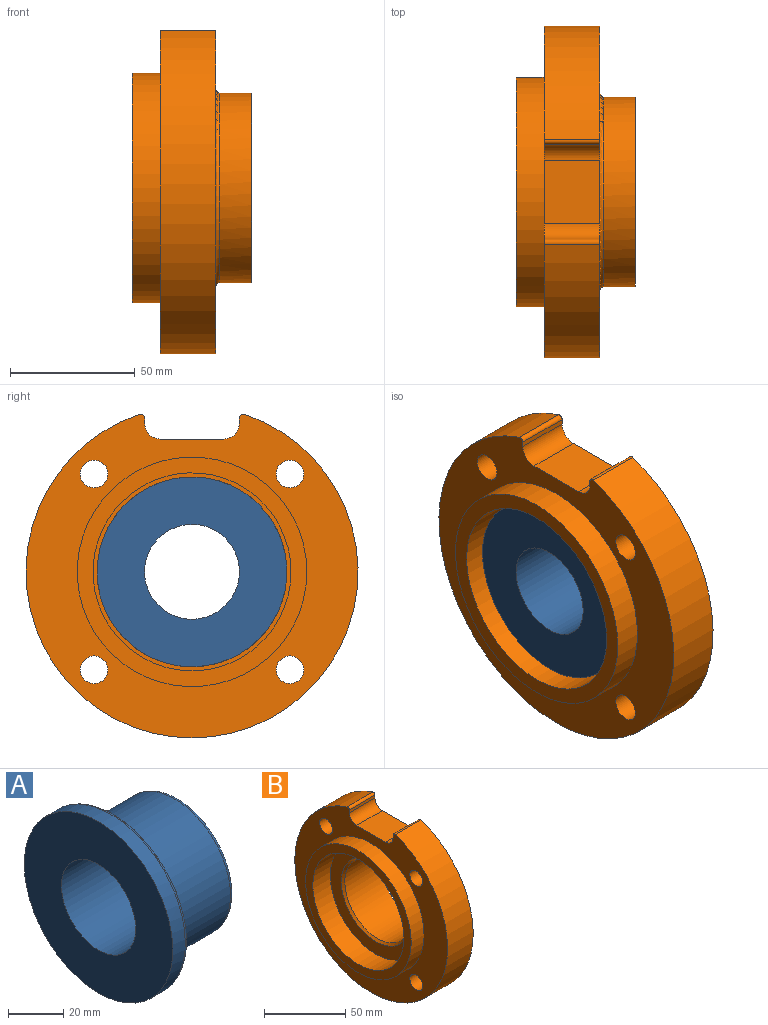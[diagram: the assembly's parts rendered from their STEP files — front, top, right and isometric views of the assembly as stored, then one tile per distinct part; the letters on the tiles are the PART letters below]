
ASSEMBLY  parts=2 mates=1
PART A: 9 faces, bbox 40.6x82.5x82.5 mm
  f0: cylinder r=19.05mm len=40.64mm, axis (-1,0,0), area 4864.4mm2, adj f3,f5
  f1: cylinder r=38.1mm len=76.2mm, axis (-1,0,0), area 1520.1mm2, adj f3,f8
  f2: plane 73.15x73.15mm, normal (1,0,0), area 1356.7mm2, adj f6,f8
  f3: plane 76.2x76.2mm, normal (-1,0,0), area 3420.3mm2, adj f0,f1
  f4: cylinder r=28.57mm len=57.15mm, axis (-1,0,0), area 5335.6mm2, adj f6,f7
  f5: plane 54.1x54.1mm, normal (1,0,0), area 1158.8mm2, adj f0,f7
  f6: torus R=30.1mm, axis (1,0,0), area 438.1mm2, adj f2,f4
  f7: torus R=27.05mm, axis (1,0,0), area 421.5mm2, adj f4,f5
  f8: torus R=36.58mm, axis (1,0,0), area 564.7mm2, adj f1,f2
PART B: 23 faces, bbox 47.8x133.4x130 mm
  f0: cylinder r=28.57mm len=57.15mm, axis (-1,0,0), area 5563.6mm2, adj f16,f22
  f1: plane 25.4x22.35mm, normal (0,0,1), area 567.7mm2, adj f2,f6,f7,f8
  f2: cylinder r=6.35mm len=22.35mm, axis (-1,0,0), area 223mm2, adj f1,f3,f7,f8
  f3: plane 22.35x2.13mm, normal (0,1,0), area 47.5mm2, adj f2,f7,f8,f9
  f4: cylinder r=66.67mm len=133.35mm, axis (-1,0,0), area 8406.3mm2, adj f7,f8,f9,f10
  f5: plane 22.35x2.13mm, normal (0,-1,0), area 47.5mm2, adj f6,f7,f8,f10
  f6: cylinder r=6.35mm len=22.35mm, axis (-1,0,0), area 223mm2, adj f1,f5,f7,f8
  f7: plane 133.35x130.02mm, normal (1,0,0), area 8187.9mm2, adj f1,f2,f3,f4,f5,f6,f9,f10
  f8: plane 133.35x130.02mm, normal (-1,0,0), area 6443.6mm2, adj f1,f2,f3,f4,f5,f6,f9,f10
  f9: cylinder r=1.52mm len=22.35mm, axis (-1,0,0), area 64.5mm2, adj f3,f4,f7,f8
  f10: cylinder r=1.52mm len=22.35mm, axis (-1,0,0), area 64.5mm2, adj f4,f5,f7,f8
  f11: cylinder r=5.56mm len=22.35mm, axis (1,0,0), area 780.3mm2, adj f7,f8
  f12: cylinder r=5.56mm len=22.35mm, axis (1,0,0), area 780.3mm2, adj f7,f8
  f13: cylinder r=5.56mm len=22.35mm, axis (1,0,0), area 780.3mm2, adj f7,f8
  f14: cylinder r=5.56mm len=22.35mm, axis (1,0,0), area 780.3mm2, adj f7,f8
  f15: cylinder r=38.1mm len=76.2mm, axis (-1,0,0), area 3040.2mm2, adj f16,f17
  f16: plane 76.2x76.2mm, normal (1,0,0), area 1995.2mm2, adj f0,f15
  f17: torus R=39.62mm, axis (1,0,0), area 581.4mm2, adj f7,f15
  f18: plane 92.2x92.2mm, normal (-1,0,0), area 1712.7mm2, adj f19,f20
  f19: cylinder r=46.1mm len=92.2mm, axis (1,0,0), area 3237.3mm2, adj f8,f18
  f20: cylinder r=39.75mm len=79.5mm, axis (-1,0,0), area 3806.4mm2, adj f18,f21
  f21: plane 79.5x79.5mm, normal (-1,0,0), area 2118mm2, adj f20,f22
  f22: cone r=28.57mm half-angle=45deg, axis (-1,0,0), area 397.3mm2, adj f0,f21
PLACE A t=(-3.81,0,0)mm
PLACE B at identity
MATE fastened A.f0 <-> B.f0  axis (1,0,0) through (4.06,0,0)mm
